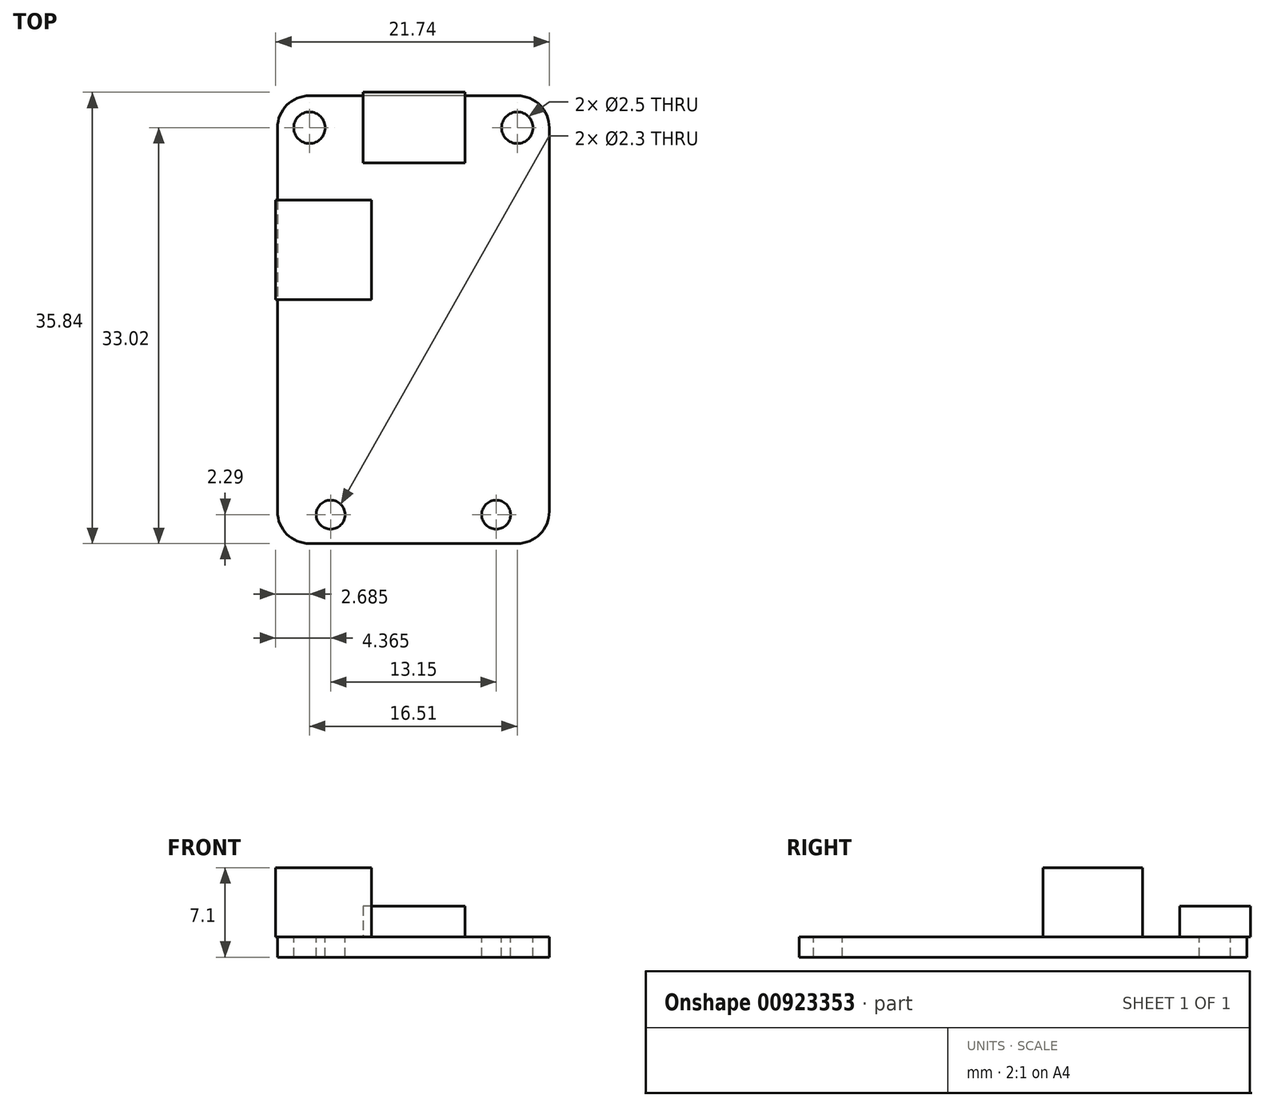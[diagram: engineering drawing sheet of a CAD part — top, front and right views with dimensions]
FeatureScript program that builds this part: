
annotation { "Feature Type Name" : "Feature", "Feature Type Description" : "" }
export const myFeature = defineFeature(function(context is Context, id is Id, definition is map)
    precondition{}
    {
        {
            var Q0;
            Q0=qCreatedBy(makeId("Top.planeOp"),FACE);
            var sketch = newSketch(context, id + "F0", { "sketchPlane" : qUnion([Q0])});
            skLineSegment(sketch, "E0.bottom", {"start": v(8.25, 17.78) * mm, "end": v(-8.26, 17.78) * mm});
            skLineSegment(sketch, "E0.top", {"start": v(8.25, -17.78) * mm, "end": v(-8.26, -17.78) * mm});
            skLineSegment(sketch, "E0.left", {"start": v(10.8, 15.24) * mm, "end": v(10.8, -15.24) * mm});
            skLineSegment(sketch, "E0.right", {"start": v(-10.8, 15.24) * mm, "end": v(-10.8, -15.24) * mm});
            skPoint(sketch, "E0.middle", {"position": v(0, 0) * mm});
            skArc(sketch, "E1", {"start": v(-8.26, 17.78) * mm, "mid": v(-10.05, 17.04) * mm, "end": v(-10.8, 15.24) * mm});
            skLineSegment(sketch, "E2", {"start": v(-10.8, 0) * mm, "end": v(10.8, 0) * mm, "construction": true});
            skLineSegment(sketch, "E3", {"start": v(0, 17.78) * mm, "end": v(0, -17.78) * mm, "construction": true});
            skArc(sketch, "E4.MirrorC", {"start": v(8.25, 17.78) * mm, "mid": v(10.05, 17.04) * mm, "end": v(10.8, 15.24) * mm});
            skArc(sketch, "E5.MirrorC", {"start": v(-8.26, -17.78) * mm, "mid": v(-10.05, -17.04) * mm, "end": v(-10.8, -15.24) * mm});
            skArc(sketch, "E6.MirrorC", {"start": v(8.25, -17.78) * mm, "mid": v(10.05, -17.04) * mm, "end": v(10.8, -15.24) * mm});
            skPoint(sketch, "E7.orphan", {"position": v(-10.8, 17.78) * mm});
            skPoint(sketch, "E8.orphan", {"position": v(10.8, 17.78) * mm});
            skPoint(sketch, "E9.orphan", {"position": v(10.8, -17.78) * mm});
            skPoint(sketch, "E10.orphan", {"position": v(-10.8, -17.78) * mm});
            skCircle(sketch, "E11.MirrorC", {"center": v(-8.26, 15.24) * mm, "radius": 1.25 * mm});
            skCircle(sketch, "E12.MirrorC", {"center": v(8.25, 15.24) * mm, "radius": 1.25 * mm});
            skCircle(sketch, "E13", {"center": v(-6.58, -15.5) * mm, "radius": 1.15 * mm});
            skCircle(sketch, "E14.MirrorC", {"center": v(6.57, -15.5) * mm, "radius": 1.15 * mm});
            skSolve(sketch);
        }
        {
            var Q0;
            Q0=makeQuery(id+"F0.imprint","IMPRINT",FACE,{"disambiguationData":[TD([[makeQuery(id+"F0.imprint","IMPRINT",EDGE,{"derivedFrom":sQuery(id+"F0.wireOp",EDGE,"E0.bottom")}),1.0]])]});
            extrude(context, id + "F1", {"entities" : qUnion([Q0]), "oppositeDirection" : true, "depth" : 1.6 * mm, "offsetDistance" : 25 * mm});
        }
        {
            var Q0;
            Q0=qCreatedBy(makeId("Top.planeOp"),FACE);
            var sketch = newSketch(context, id + "F2", { "sketchPlane" : qUnion([Q0])});
            skLineSegment(sketch, "E15.0.0", {"start": v(-8.26, -17.78) * mm, "end": v(8.25, -17.78) * mm, "construction": true});
            skArc(sketch, "E15.0.1", {"start": v(8.25, -17.78) * mm, "mid": v(10.05, -17.04) * mm, "end": v(10.8, -15.24) * mm, "construction": true});
            skLineSegment(sketch, "E15.0.2", {"start": v(10.8, -15.24) * mm, "end": v(10.8, 15.24) * mm, "construction": true});
            skArc(sketch, "E15.0.3", {"start": v(10.8, 15.24) * mm, "mid": v(10.05, 17.04) * mm, "end": v(8.25, 17.78) * mm, "construction": true});
            skLineSegment(sketch, "E15.0.4", {"start": v(8.25, 17.78) * mm, "end": v(-8.26, 17.78) * mm, "construction": true});
            skArc(sketch, "E15.0.5", {"start": v(-8.26, 17.78) * mm, "mid": v(-10.05, 17.04) * mm, "end": v(-10.8, 15.24) * mm, "construction": true});
            skLineSegment(sketch, "E15.0.6", {"start": v(-10.8, 15.24) * mm, "end": v(-10.8, -15.24) * mm, "construction": true});
            skArc(sketch, "E15.0.7", {"start": v(-10.8, -15.24) * mm, "mid": v(-10.05, -17.04) * mm, "end": v(-8.26, -17.78) * mm, "construction": true});
            skLineSegment(sketch, "E16.bottom", {"start": v(-3.34, 1.6) * mm, "end": v(-10.94, 1.6) * mm});
            skLineSegment(sketch, "E16.top", {"start": v(-3.34, 9.5) * mm, "end": v(-10.94, 9.5) * mm});
            skLineSegment(sketch, "E16.left", {"start": v(-3.34, 1.6) * mm, "end": v(-3.34, 9.5) * mm});
            skLineSegment(sketch, "E16.right", {"start": v(-10.94, 1.6) * mm, "end": v(-10.94, 9.5) * mm});
            skPoint(sketch, "E16.middle", {"position": v(-7.14, 5.54) * mm});
            skSolve(sketch);
        }
        {
            var Q0;
            Q0=makeQuery(id+"F2.imprint","IMPRINT",FACE,{"disambiguationData":[TD([[makeQuery(id+"F2.imprint","IMPRINT",EDGE,{"derivedFrom":sQuery(id+"F2.wireOp",EDGE,"E16.bottom")}),-1.0]])]});
            extrude(context, id + "F3", {"entities" : qUnion([Q0]), "operationType" : NewBodyOperationType.ADD, "depth" : 5.5 * mm, "offsetDistance" : 25 * mm});
        }
        {
            var Q0;
            Q0=makeQuery(id+"F1.opExtrude","CAP_FACE",FACE,{"disambiguationData":[OSD([sQuery(id+"F0.wireOp",EDGE,"E0.bottom"),sQuery(id+"F0.wireOp",EDGE,"E0.top"),sQuery(id+"F0.wireOp",EDGE,"E0.left"),sQuery(id+"F0.wireOp",EDGE,"E0.right"),sQuery(id+"F0.wireOp",EDGE,"E1"),sQuery(id+"F0.wireOp",EDGE,"E4.MirrorC"),sQuery(id+"F0.wireOp",EDGE,"E5.MirrorC"),sQuery(id+"F0.wireOp",EDGE,"E6.MirrorC"),sQuery(id+"F0.wireOp",EDGE,"E11.MirrorC"),sQuery(id+"F0.wireOp",EDGE,"E12.MirrorC"),sQuery(id+"F0.wireOp",EDGE,"E13"),sQuery(id+"F0.wireOp",EDGE,"E14.MirrorC")])],"isStart":true});
            var sketch = newSketch(context, id + "F4", { "sketchPlane" : qUnion([Q0])});
            skLineSegment(sketch, "E17.bottom", {"start": v(4.1, 12.46) * mm, "end": v(-3.99, 12.46) * mm});
            skLineSegment(sketch, "E17.top", {"start": v(4.1, 18.06) * mm, "end": v(-3.99, 18.06) * mm});
            skLineSegment(sketch, "E17.left", {"start": v(4.1, 12.46) * mm, "end": v(4.1, 18.06) * mm});
            skLineSegment(sketch, "E17.right", {"start": v(-3.99, 12.46) * mm, "end": v(-3.99, 18.06) * mm});
            skPoint(sketch, "E17.middle", {"position": v(0.06, 15.26) * mm});
            skLineSegment(sketch, "E18.0.0", {"start": v(-3.34, 9.5) * mm, "end": v(-3.34, 1.6) * mm, "construction": true});
            skLineSegment(sketch, "E18.0.1", {"start": v(-3.34, 1.6) * mm, "end": v(-10.8, 1.6) * mm, "construction": true});
            skLineSegment(sketch, "E18.0.2", {"start": v(-10.8, 1.6) * mm, "end": v(-10.8, -15.24) * mm, "construction": true});
            skArc(sketch, "E18.0.3", {"start": v(-10.8, -15.24) * mm, "mid": v(-10.05, -17.04) * mm, "end": v(-8.26, -17.78) * mm, "construction": true});
            skLineSegment(sketch, "E18.0.4", {"start": v(-8.26, -17.78) * mm, "end": v(8.25, -17.78) * mm, "construction": true});
            skArc(sketch, "E18.0.5", {"start": v(8.25, -17.78) * mm, "mid": v(10.05, -17.04) * mm, "end": v(10.8, -15.24) * mm, "construction": true});
            skLineSegment(sketch, "E18.0.6", {"start": v(10.8, -15.24) * mm, "end": v(10.8, 15.24) * mm, "construction": true});
            skArc(sketch, "E18.0.7", {"start": v(10.8, 15.24) * mm, "mid": v(10.05, 17.04) * mm, "end": v(8.25, 17.78) * mm, "construction": true});
            skLineSegment(sketch, "E18.0.8", {"start": v(8.25, 17.78) * mm, "end": v(-8.26, 17.78) * mm, "construction": true});
            skArc(sketch, "E18.0.9", {"start": v(-8.26, 17.78) * mm, "mid": v(-10.05, 17.04) * mm, "end": v(-10.8, 15.24) * mm, "construction": true});
            skLineSegment(sketch, "E18.0.10", {"start": v(-10.8, 15.24) * mm, "end": v(-10.8, 9.5) * mm, "construction": true});
            skLineSegment(sketch, "E18.0.11", {"start": v(-10.8, 9.5) * mm, "end": v(-3.34, 9.5) * mm, "construction": true});
            skSolve(sketch);
        }
        {
            var Q0;
            {var subQ0=sQuery(id+"F4.wireOp",EDGE,"E17.top");Q0=makeQuery(id+"F4.imprint","IMPRINT",FACE,{"disambiguationData":[TD([[makeQuery(id+"F4.imprint","IMPRINT",EDGE,{"derivedFrom":subQ0}),1.0]])]});}
            var Q1;
            {var subQ0=sQuery(id+"F4.wireOp",EDGE,"E17.bottom");Q1=makeQuery(id+"F4.imprint","IMPRINT",FACE,{"disambiguationData":[TD([[makeQuery(id+"F4.imprint","IMPRINT",EDGE,{"derivedFrom":subQ0}),-1.0]])]});}
            extrude(context, id + "F5", {"entities" : qUnion([Q0, Q1]), "operationType" : NewBodyOperationType.ADD, "depth" : 2.45 * mm, "offsetDistance" : 25 * mm});
        }
    });
